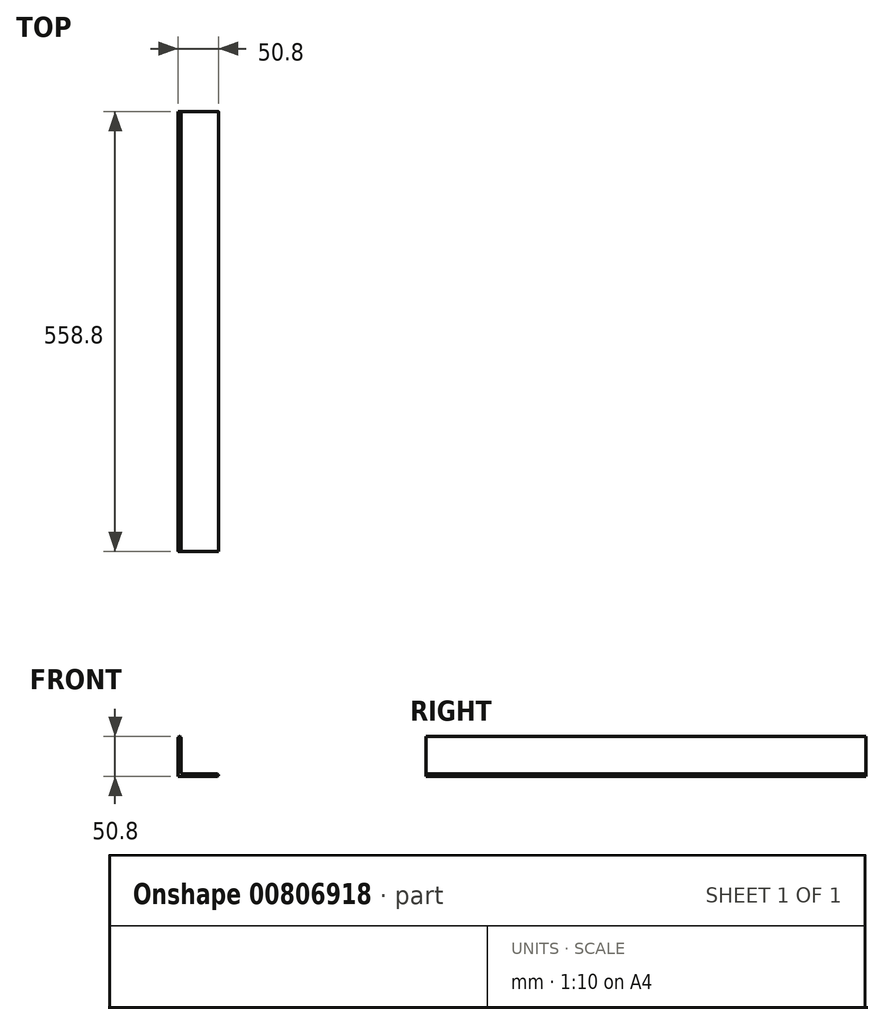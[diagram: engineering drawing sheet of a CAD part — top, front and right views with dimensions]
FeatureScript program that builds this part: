
annotation { "Feature Type Name" : "Feature", "Feature Type Description" : "" }
export const myFeature = defineFeature(function(context is Context, id is Id, definition is map)
    precondition{}
    {
        {
            var Q0;
            Q0=qCreatedBy(makeId("Front.planeOp"),FACE);
            var sketch = newSketch(context, id + "F0", { "sketchPlane" : qUnion([Q0])});
            skLineSegment(sketch, "E0.bottom", {"start": v(0, 0) * mm, "end": v(49.28, 0) * mm});
            skLineSegment(sketch, "E0.top", {"start": v(1.52, 50.8) * mm, "end": v(1.65, 50.8) * mm});
            skLineSegment(sketch, "E0.left", {"start": v(0, 0) * mm, "end": v(0, 49.28) * mm});
            skLineSegment(sketch, "E0.right", {"start": v(50.8, 1.52) * mm, "end": v(50.8, 1.65) * mm});
            skLineSegment(sketch, "E1.0", {"start": v(3.17, 6.35) * mm, "end": v(3.17, 49.28) * mm});
            skLineSegment(sketch, "E1.1", {"start": v(6.35, 3.18) * mm, "end": v(49.28, 3.18) * mm});
            skPoint(sketch, "E2.visualSharp", {"position": v(3.17, 3.18) * mm});
            skArc(sketch, "E2.filletArc", {"start": v(3.17, 6.35) * mm, "mid": v(4.1, 4.1) * mm, "end": v(6.35, 3.17) * mm});
            skPoint(sketch, "E3.visualSharp", {"position": v(0, 50.8) * mm});
            skArc(sketch, "E3.filletArc", {"start": v(1.52, 50.8) * mm, "mid": v(0.45, 50.35) * mm, "end": v(0, 49.28) * mm});
            skPoint(sketch, "E4.visualSharp", {"position": v(50.8, 0) * mm});
            skArc(sketch, "E4.filletArc", {"start": v(49.28, 0) * mm, "mid": v(50.35, 0.45) * mm, "end": v(50.8, 1.52) * mm});
            skPoint(sketch, "E5.visualSharp", {"position": v(50.8, 3.18) * mm});
            skArc(sketch, "E5.filletArc", {"start": v(50.8, 1.65) * mm, "mid": v(50.35, 2.73) * mm, "end": v(49.28, 3.18) * mm});
            skPoint(sketch, "E6.visualSharp", {"position": v(3.17, 50.8) * mm});
            skArc(sketch, "E6.filletArc", {"start": v(3.17, 49.28) * mm, "mid": v(2.73, 50.35) * mm, "end": v(1.65, 50.8) * mm});
            skSolve(sketch);
        }
        {
            var Q0;
            Q0 = qSketchRegion(id + "F0", true);
            extrude(context, id + "F1", {"entities" : qUnion([Q0]), "depth" : 558.8 * mm, "offsetDistance" : 25.4 * mm});
        }
    });
